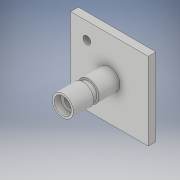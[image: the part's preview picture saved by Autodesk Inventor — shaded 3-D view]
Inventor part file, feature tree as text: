
AUTODESK INVENTOR PART (.ipt)
format: ipt  version: 2019 (Build 230136000, 136)  size: 302,592 bytes
history: native  units: in
note: dims shown in document units (in); Inventor stores cm internally (conversion verified against a paired STEP export)
features: sketch x7, extrude x6, other x1, plane x1
ambient origin geometry x8: Origin, YZ Plane, XZ Plane, XY Plane, X Axis, Y Axis, Z Axis, Center Point
bodies: Body1 (feature_tree)
feature tree (15):
  other  "Sólido1"
  extrude  "Extrusión1"  Depth=1.1811in TaperAngle=0.0deg
  plane  "Plano de trabajo1"
  extrude  "Extrusión2"  Depth=0.4331in
  extrude  "Extrusión3"  Depth=0.1378in TaperAngle=0.0deg
  sketch  "Boceto4"  dims[d8=1.9685in d9=1.9685in]
  extrude  "Extrusión4"  Depth=1.9685in
  extrude  "Extrusión5"  Depth=0.1969in
  extrude  "Extrusión6"  Depth=0.1535in
  sketch  "Boceto1"  dims[d0=0.5354in d1=1.1811in d2=0.0in]
  sketch  "Boceto2"  dims[d3=-0.5315in d4=0.4331in]
  sketch  "Boceto3"  dims[d5=0.5512in d6=0.1378in d7=0.0in]
  sketch  "Boceto5"  dims[d18=0.1969in d19=0.1969in]
  sketch  "Boceto6"  dims[d20=0.1535in d21=0.1535in]
  sketch  "Boceto7"  dims[d22=0.1969in d23=0.0in d24=0.3248in d25=0.3169in d26=0.3248in d27=0.3173in d28=0.3248in d29=0.3169in d30=0.3248in d31=0.3169in d32=0.2362in d33=1.2992in d34=0.0in d35=0.4331in d36=0.1575in d37=0.0in d38=0.3937in d39=0.0in]
